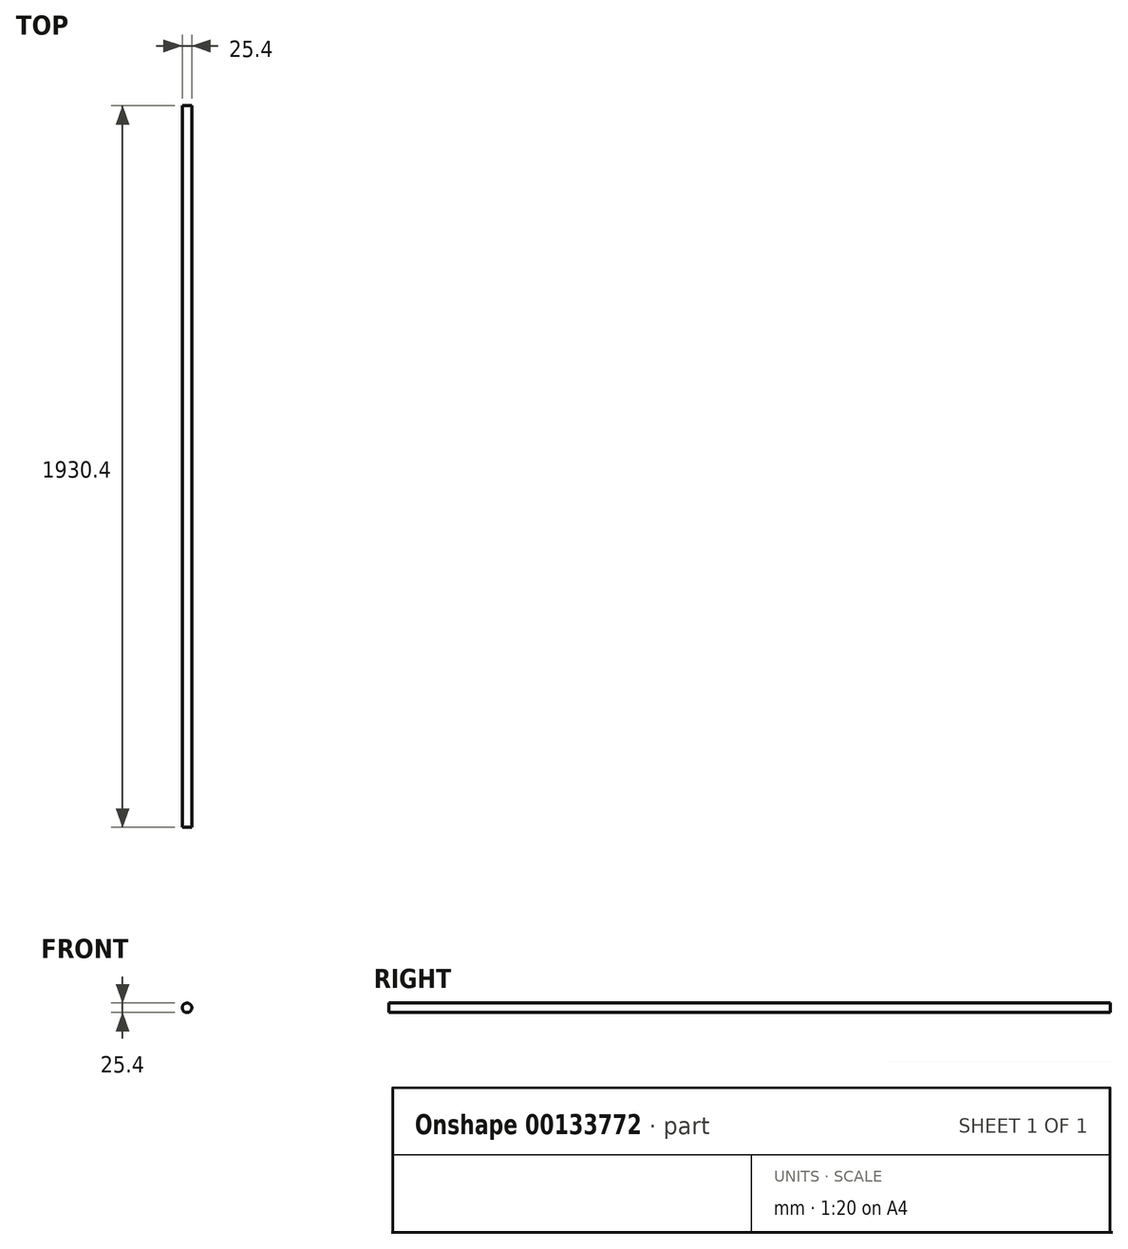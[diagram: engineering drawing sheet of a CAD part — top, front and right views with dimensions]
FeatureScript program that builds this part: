
annotation { "Feature Type Name" : "Feature", "Feature Type Description" : "" }
export const myFeature = defineFeature(function(context is Context, id is Id, definition is map)
    precondition{}
    {
        {
            var Q0;
            Q0=qCreatedBy(makeId("Front.planeOp"),FACE);
            var sketch = newSketch(context, id + "F0", { "sketchPlane" : qUnion([Q0])});
            skCircle(sketch, "E0", {"center": v(-34.6, 68.92) * mm, "radius": 12.7 * mm});
            skSolve(sketch);
        }
        {
            var Q0;
            Q0=makeQuery(id+"F0.imprint","IMPRINT",FACE,{"disambiguationData":[TD([[makeQuery(id+"F0.imprint","IMPRINT",EDGE,{"derivedFrom":sQuery(id+"F0.wireOp",EDGE,"E0")}),1.0]])]});
            var Q1;
            Q1=sQuery(id+"F0.wireOp",EDGE,"E0");
            extrude(context, id + "F1", {"entities" : qUnion([Q0]), "surfaceEntities" : qUnion([Q1]), "depth" : 1930.4 * mm});
        }
    });
